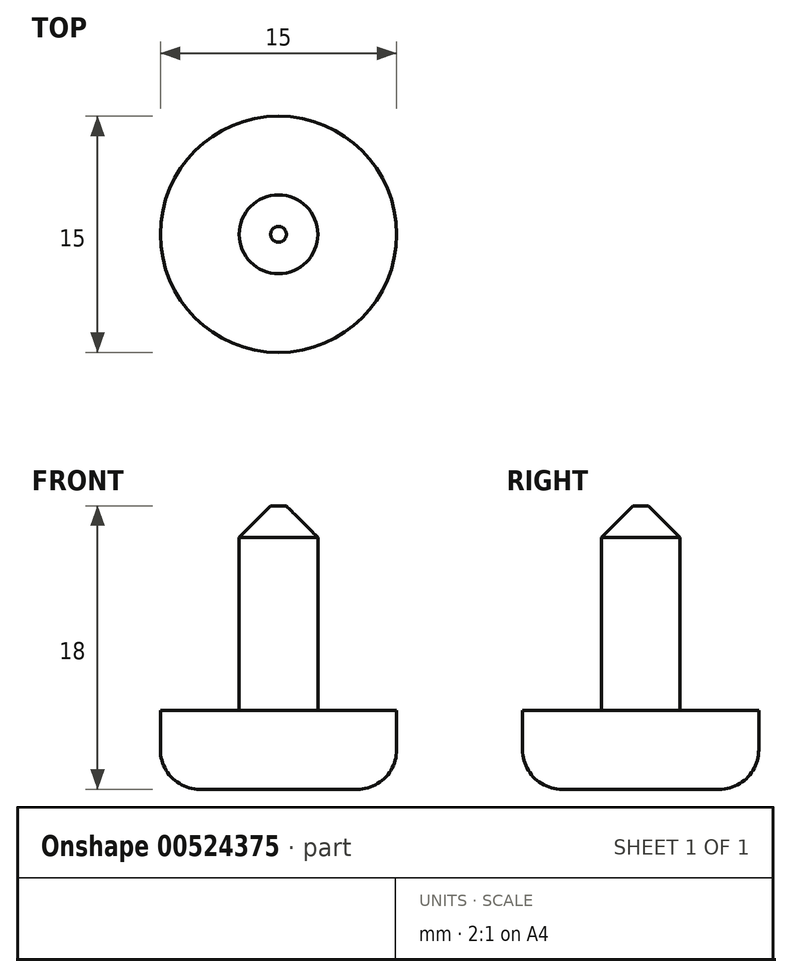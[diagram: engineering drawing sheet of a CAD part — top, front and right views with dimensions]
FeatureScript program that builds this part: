
annotation { "Feature Type Name" : "Feature", "Feature Type Description" : "" }
export const myFeature = defineFeature(function(context is Context, id is Id, definition is map)
    precondition{}
    {
        {
            var Q0;
            Q0=qCreatedBy(makeId("Top.planeOp"),FACE);
            var sketch = newSketch(context, id + "F0", { "sketchPlane" : qUnion([Q0])});
            skCircle(sketch, "E0", {"center": v(0, 0) * mm, "radius": 7.5 * mm});
            skSolve(sketch);
        }
        {
            var Q0;
            Q0 = qSketchRegion(id + "F0", true);
            extrude(context, id + "F1", {"entities" : qUnion([Q0]), "depth" : 5 * mm, "offsetDistance" : 25 * mm});
        }
        {
            var Q0;
            Q0=makeQuery(id+"F1.opExtrude","CAP_FACE",FACE,{"disambiguationData":[OSD([sQuery(id+"F0.wireOp",EDGE,"E0")])],"isStart":false});
            var sketch = newSketch(context, id + "F2", { "sketchPlane" : qUnion([Q0])});
            skCircle(sketch, "E1", {"center": v(0, 0) * mm, "radius": 2.5 * mm});
            skSolve(sketch);
        }
        {
            var Q0;
            Q0 = qSketchRegion(id + "F2", true);
            extrude(context, id + "F3", {"entities" : qUnion([Q0]), "operationType" : NewBodyOperationType.ADD, "depth" : (5 + 8) * mm, "offsetDistance" : 25 * mm});
        }
        {
            var Q0;
            Q0=makeQuery(id+"F1.opExtrude","CAP_EDGE",EDGE,{"disambiguationData":[OSD([sQuery(id+"F0.wireOp",EDGE,"E0")])],"isStart":true});
            fillet(context, id + "F4", {"entities" : qUnion([Q0]), "radius" : 2.5 * mm, "tangentPropagation" : true, "allowEdgeOverflow" : false});
        }
        {
            var Q0;
            Q0=makeQuery(id+"F3.opExtrude","CAP_EDGE",EDGE,{"disambiguationData":[OSD([sQuery(id+"F2.wireOp",EDGE,"E1")])],"isStart":false});
            chamfer(context, id + "F5", {"entities" : qUnion([Q0]), "width" : 2 * mm, "tangentPropagation" : true});
        }
    });
